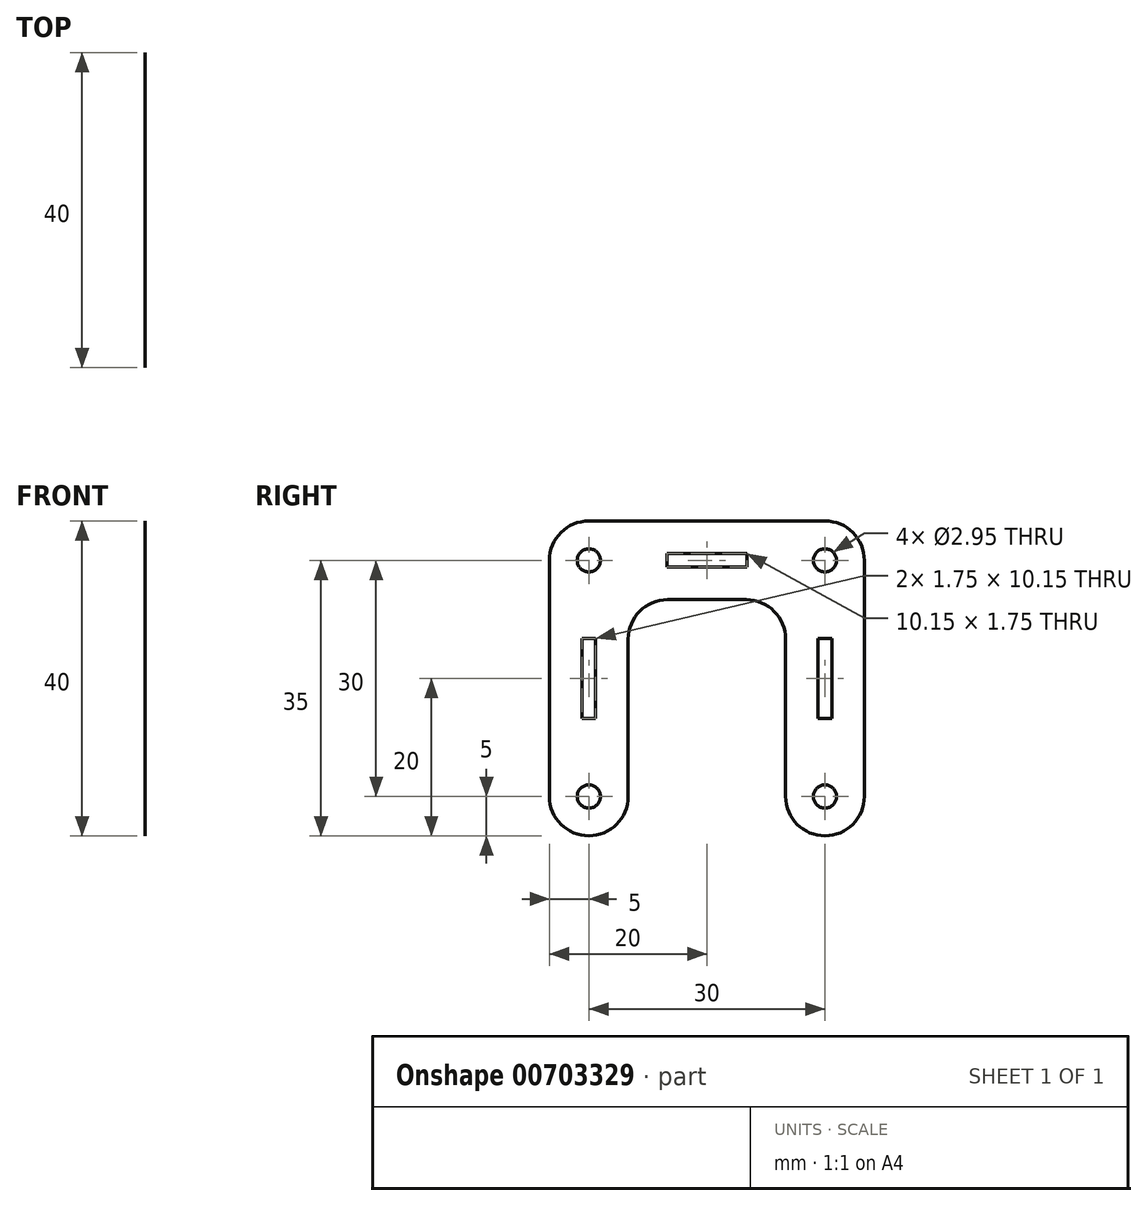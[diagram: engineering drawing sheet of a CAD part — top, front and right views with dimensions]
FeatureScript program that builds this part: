
annotation { "Feature Type Name" : "Feature", "Feature Type Description" : "" }
export const myFeature = defineFeature(function(context is Context, id is Id, definition is map)
    precondition{}
    {
        {
            var Q0;
            Q0=qCreatedBy(makeId("Right.planeOp"),FACE);
            var sketch = newSketch(context, id + "F0", { "sketchPlane" : qUnion([Q0])});
            skLineSegment(sketch, "E0.bottom", {"start": v(20, 20) * mm, "end": v(-20, 20) * mm});
            skLineSegment(sketch, "E0.top", {"start": v(20, -20) * mm, "end": v(-20, -20) * mm});
            skLineSegment(sketch, "E0.left", {"start": v(20, 20) * mm, "end": v(20, -20) * mm});
            skLineSegment(sketch, "E0.right", {"start": v(-20, 20) * mm, "end": v(-20, -20) * mm});
            skPoint(sketch, "E0.middle", {"position": v(0, 0) * mm});
            skCircle(sketch, "E1", {"center": v(-15, 15) * mm, "radius": 1.47 * mm});
            skCircle(sketch, "E2", {"center": v(15, 15) * mm, "radius": 1.47 * mm});
            skCircle(sketch, "E3", {"center": v(15, -15) * mm, "radius": 1.47 * mm});
            skCircle(sketch, "E4", {"center": v(-15, -15) * mm, "radius": 1.47 * mm});
            skCircle(sketch, "E5", {"center": v(0, 0) * mm, "radius": 6.35 * mm});
            skLineSegment(sketch, "E6", {"start": v(-10, -20) * mm, "end": v(-10, 10) * mm});
            skLineSegment(sketch, "E7", {"start": v(-10, 10) * mm, "end": v(10, 10) * mm});
            skLineSegment(sketch, "E8", {"start": v(10, 10) * mm, "end": v(10, -20) * mm});
            skLineSegment(sketch, "E9.bottom", {"start": v(5.08, 15.87) * mm, "end": v(-5.08, 15.87) * mm});
            skLineSegment(sketch, "E9.top", {"start": v(5.08, 14.13) * mm, "end": v(-5.08, 14.13) * mm});
            skLineSegment(sketch, "E9.left", {"start": v(5.08, 15.87) * mm, "end": v(5.08, 14.13) * mm});
            skLineSegment(sketch, "E9.right", {"start": v(-5.08, 15.87) * mm, "end": v(-5.08, 14.13) * mm});
            skPoint(sketch, "E9.middle", {"position": v(0, 15) * mm});
            skLineSegment(sketch, "E10.bottom", {"start": v(14.13, -5.08) * mm, "end": v(15.87, -5.08) * mm});
            skLineSegment(sketch, "E10.top", {"start": v(14.13, 5.08) * mm, "end": v(15.87, 5.08) * mm});
            skLineSegment(sketch, "E10.left", {"start": v(14.13, -5.08) * mm, "end": v(14.13, 5.08) * mm});
            skLineSegment(sketch, "E10.right", {"start": v(15.87, -5.08) * mm, "end": v(15.87, 5.08) * mm});
            skPoint(sketch, "E10.middle", {"position": v(15, 0) * mm});
            skLineSegment(sketch, "E11.bottom", {"start": v(-14.13, -5.07) * mm, "end": v(-15.87, -5.07) * mm});
            skLineSegment(sketch, "E11.top", {"start": v(-14.13, 5.08) * mm, "end": v(-15.87, 5.08) * mm});
            skLineSegment(sketch, "E11.left", {"start": v(-14.13, -5.07) * mm, "end": v(-14.13, 5.08) * mm});
            skLineSegment(sketch, "E11.right", {"start": v(-15.87, -5.07) * mm, "end": v(-15.87, 5.08) * mm});
            skPoint(sketch, "E11.middle", {"position": v(-15, 0) * mm});
            skSolve(sketch);
        }
        {
            var Q0;
            Q0=makeQuery(id+"F0.imprint","IMPRINT",FACE,{"disambiguationData":[TD([[makeQuery(id+"F0.imprint","IMPRINT",EDGE,{"derivedFrom":sQuery(id+"F0.wireOp",EDGE,"E0.bottom")}),1.0]])]});
            extrude(context, id + "F1", {"entities" : qUnion([Q0]), "depth" : 1 / 406.4 * mm, "offsetDistance" : 25 * mm});
        }
        {
            var Q0;
            Q0=makeQuery(id+"F1.opExtrude","SWEPT_EDGE",EDGE,{"disambiguationData":[OSD([sQuery(id+"F0.wireOp",EDGE,"E0.bottom"),sQuery(id+"F0.wireOp",EDGE,"E0.right")])]});
            var Q1;
            Q1=makeQuery(id+"F1.opExtrude","SWEPT_EDGE",EDGE,{"disambiguationData":[OSD([sQuery(id+"F0.wireOp",EDGE,"E0.top"),sQuery(id+"F0.wireOp",EDGE,"E0.right")])]});
            var Q2;
            Q2=makeQuery(id+"F1.opExtrude","SWEPT_EDGE",EDGE,{"disambiguationData":[OSD([sQuery(id+"F0.wireOp",EDGE,"E6"),sQuery(id+"F0.wireOp",EDGE,"E7")])]});
            var Q3;
            Q3=makeQuery(id+"F1.opExtrude","SWEPT_EDGE",EDGE,{"disambiguationData":[OSD([sQuery(id+"F0.wireOp",EDGE,"E0.top"),sQuery(id+"F0.wireOp",EDGE,"E6")])]});
            var Q4;
            Q4=makeQuery(id+"F1.opExtrude","SWEPT_EDGE",EDGE,{"disambiguationData":[OSD([sQuery(id+"F0.wireOp",EDGE,"E0.top"),sQuery(id+"F0.wireOp",EDGE,"E8")])]});
            var Q5;
            Q5=makeQuery(id+"F1.opExtrude","SWEPT_EDGE",EDGE,{"disambiguationData":[OSD([sQuery(id+"F0.wireOp",EDGE,"E0.top"),sQuery(id+"F0.wireOp",EDGE,"E0.left")])]});
            var Q6;
            Q6=makeQuery(id+"F1.opExtrude","SWEPT_EDGE",EDGE,{"disambiguationData":[OSD([sQuery(id+"F0.wireOp",EDGE,"E7"),sQuery(id+"F0.wireOp",EDGE,"E8")])]});
            var Q7;
            Q7=makeQuery(id+"F1.opExtrude","SWEPT_EDGE",EDGE,{"disambiguationData":[OSD([sQuery(id+"F0.wireOp",EDGE,"E0.bottom"),sQuery(id+"F0.wireOp",EDGE,"E0.left")])]});
            fillet(context, id + "F2", {"entities" : qUnion([Q0, Q1, Q2, Q3, Q4, Q5, Q6, Q7]), "radius" : 5 * mm, "tangentPropagation" : true, "allowEdgeOverflow" : false});
        }
    });
